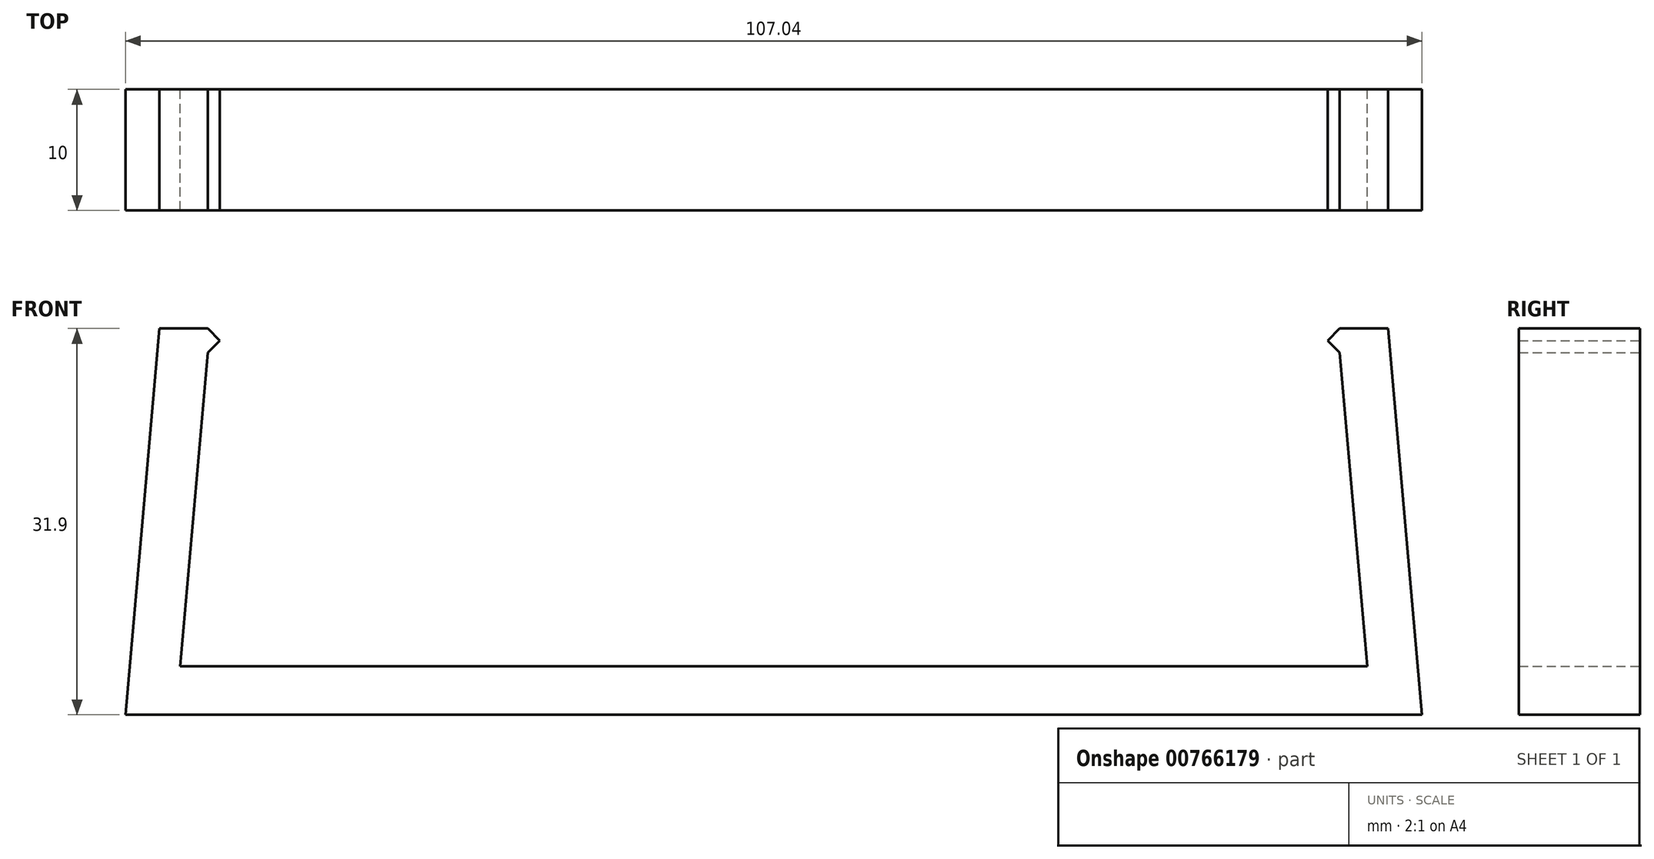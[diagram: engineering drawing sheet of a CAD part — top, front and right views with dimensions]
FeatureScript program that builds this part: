
annotation { "Feature Type Name" : "Feature", "Feature Type Description" : "" }
export const myFeature = defineFeature(function(context is Context, id is Id, definition is map)
    precondition{}
    {
        {
            var Q0;
            Q0=qCreatedBy(makeId("Front.planeOp"),FACE);
            var sketch = newSketch(context, id + "F0", { "sketchPlane" : qUnion([Q0])});
            skLineSegment(sketch, "E0", {"start": v(0, 0) * mm, "end": v(53.52, 0) * mm});
            skLineSegment(sketch, "E1", {"start": v(53.52, 0) * mm, "end": v(50.73, 31.9) * mm});
            skLineSegment(sketch, "E2", {"start": v(50.73, 31.9) * mm, "end": v(46.73, 31.9) * mm});
            skLineSegment(sketch, "E3", {"start": v(46.73, 31.9) * mm, "end": v(45.73, 30.9) * mm});
            skLineSegment(sketch, "E4", {"start": v(45.73, 30.9) * mm, "end": v(46.73, 29.9) * mm});
            skLineSegment(sketch, "E5", {"start": v(46.73, 29.9) * mm, "end": v(49, 4) * mm});
            skLineSegment(sketch, "E6", {"start": v(49, 4) * mm, "end": v(0, 4) * mm});
            skLineSegment(sketch, "E7", {"start": v(0, 0) * mm, "end": v(0, 23.7) * mm, "construction": true});
            skLineSegment(sketch, "E8.MirrorCS", {"start": v(-45.73, 30.9) * mm, "end": v(-46.73, 29.9) * mm});
            skLineSegment(sketch, "E9.MirrorCS", {"start": v(-46.73, 31.9) * mm, "end": v(-45.73, 30.9) * mm});
            skLineSegment(sketch, "E10.MirrorCS", {"start": v(0, 0) * mm, "end": v(-53.52, 0) * mm});
            skLineSegment(sketch, "E11.MirrorCS", {"start": v(-53.52, 0) * mm, "end": v(-50.73, 31.9) * mm});
            skLineSegment(sketch, "E12.MirrorCS", {"start": v(-49, 4) * mm, "end": v(0, 4) * mm});
            skLineSegment(sketch, "E13.MirrorCS", {"start": v(-50.73, 31.9) * mm, "end": v(-46.73, 31.9) * mm});
            skLineSegment(sketch, "E14.MirrorCS", {"start": v(-46.73, 29.9) * mm, "end": v(-49, 4) * mm});
            skSolve(sketch);
        }
        {
            var Q0;
            Q0 = qSketchRegion(id + "F0", true);
            extrude(context, id + "F1", {"entities" : qUnion([Q0]), "depth" : 10 * mm, "offsetDistance" : 25 * mm});
        }
    });
